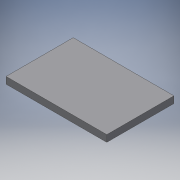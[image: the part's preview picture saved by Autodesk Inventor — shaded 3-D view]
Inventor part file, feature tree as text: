
AUTODESK INVENTOR PART (.ipt)
format: ipt  version: 2016 (Build 200138000, 138)  size: 98,304 bytes
history: native  units: in
note: dims shown in document units (in); Inventor stores cm internally (conversion verified against a paired STEP export)
features: extrude x2, sketch x2
ambient origin geometry x8: Origin, YZ Plane, XZ Plane, XY Plane, X Axis, Y Axis, Z Axis, Center Point
bodies: Solid1 (feature_tree)
feature tree (4):
  extrude  "Extrusion1"  Depth=0.5906in
  extrude  "Extrusion2"  Depth=0.1575in
  sketch  "Sketch1"  dims[d0=0.0197in d1=0.5906in]
  sketch  "Sketch2"  dims[d2=0.3937in d3=0.0in d4=0.1575in d5=0.0787in d6=0.0197in d7=0.0in]
